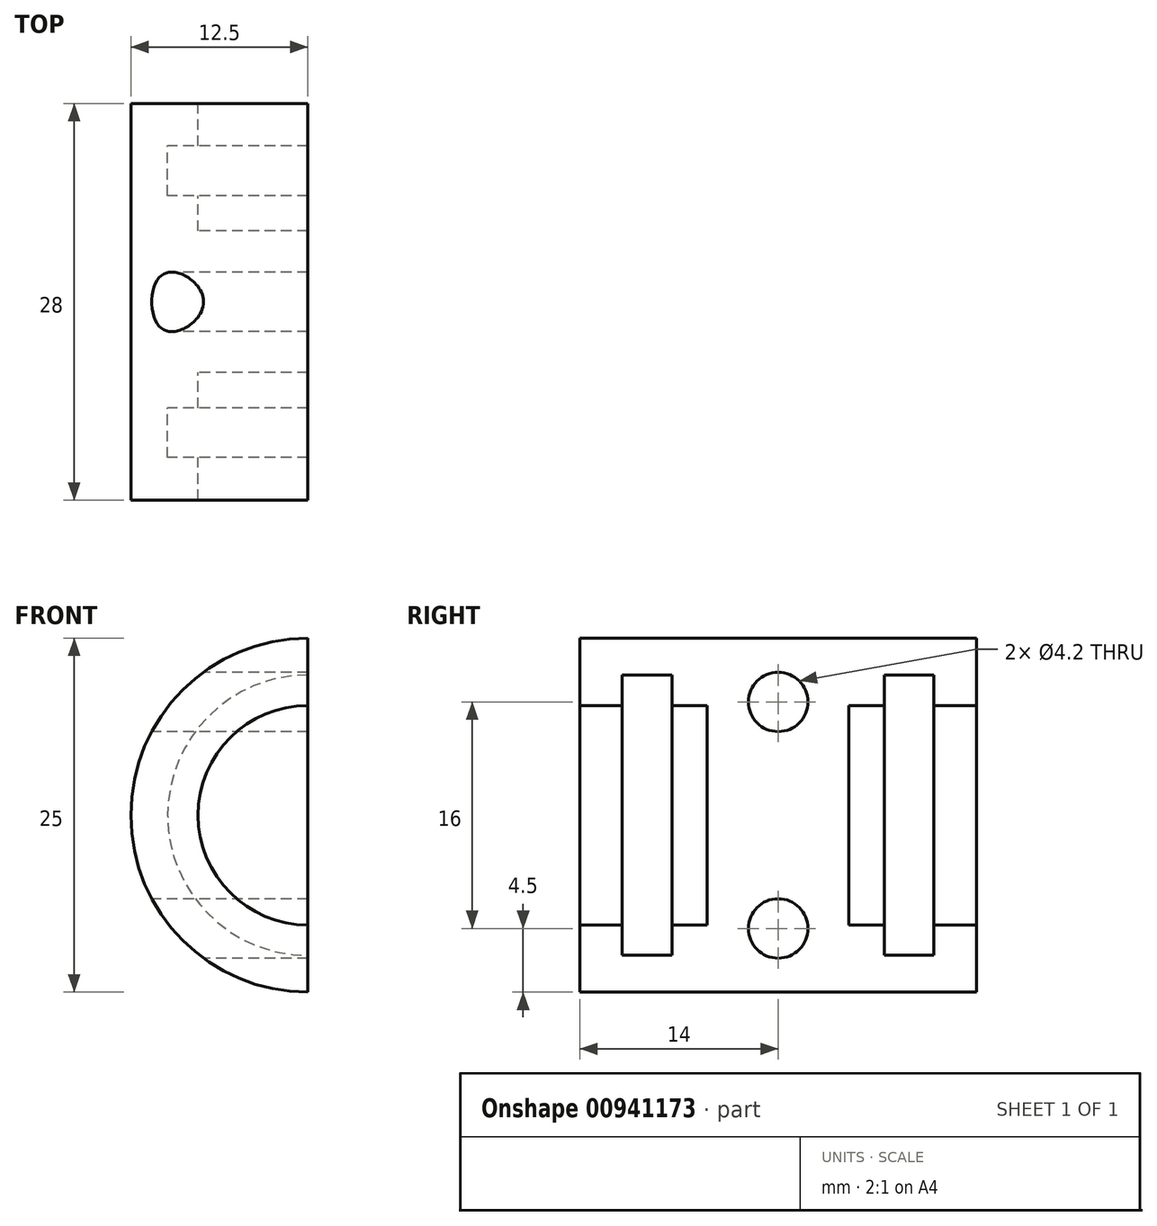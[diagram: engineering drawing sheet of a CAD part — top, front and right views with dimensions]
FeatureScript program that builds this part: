
annotation { "Feature Type Name" : "Feature", "Feature Type Description" : "" }
export const myFeature = defineFeature(function(context is Context, id is Id, definition is map)
    precondition{}
    {
        {
            var Q0;
            Q0=qCreatedBy(makeId("Front.planeOp"),FACE);
            var sketch = newSketch(context, id + "F0", { "sketchPlane" : qUnion([Q0])});
            skCircle(sketch, "E0", {"center": v(0, 0) * mm, "radius": 12.5 * mm});
            skCircle(sketch, "E1", {"center": v(0, 0) * mm, "radius": 7.75 * mm});
            skSolve(sketch);
        }
        {
            var Q0;
            Q0=makeQuery(id+"F0.imprint","IMPRINT",FACE,{"disambiguationData":[TD([[makeQuery(id+"F0.imprint","IMPRINT",EDGE,{"derivedFrom":sQuery(id+"F0.wireOp",EDGE,"E0")}),1.0]])]});
            extrude(context, id + "F1", {"entities" : qUnion([Q0]), "depth" : 28 * mm, "offsetDistance" : 25 * mm});
        }
        {
            var Q0;
            Q0=qCreatedBy(makeId("Right.planeOp"),FACE);
            var sketch = newSketch(context, id + "F2", { "sketchPlane" : qUnion([Q0])});
            skLineSegment(sketch, "E2.bottom", {"start": v(-21.5, 9.9) * mm, "end": v(-25, 9.9) * mm});
            skLineSegment(sketch, "E2.top", {"start": v(-21.5, -9.9) * mm, "end": v(-25, -9.9) * mm});
            skLineSegment(sketch, "E2.left", {"start": v(-21.5, 9.9) * mm, "end": v(-21.5, -9.9) * mm});
            skLineSegment(sketch, "E2.right", {"start": v(-25, 9.9) * mm, "end": v(-25, -9.9) * mm});
            skPoint(sketch, "E2.middle", {"position": v(-23.25, 0) * mm});
            skLineSegment(sketch, "E3.bottom", {"start": v(-3, 9.9) * mm, "end": v(-6.5, 9.9) * mm});
            skLineSegment(sketch, "E3.top", {"start": v(-3, -9.9) * mm, "end": v(-6.5, -9.9) * mm});
            skLineSegment(sketch, "E3.left", {"start": v(-3, 9.9) * mm, "end": v(-3, -9.9) * mm});
            skLineSegment(sketch, "E3.right", {"start": v(-6.5, 9.9) * mm, "end": v(-6.5, -9.9) * mm});
            skPoint(sketch, "E3.middle", {"position": v(-4.75, 0) * mm});
            skLineSegment(sketch, "E4", {"start": v(-23.25, 0) * mm, "end": v(21.1, 0) * mm});
            skLineSegment(sketch, "E5", {"start": v(21.1, 0) * mm, "end": v(-23.25, 0) * mm});
            skLineSegment(sketch, "E6", {"start": v(-34.97, 0) * mm, "end": v(-23.25, 0) * mm});
            skLineSegment(sketch, "E7", {"start": v(-32.13, 2.52) * mm, "end": v(11.78, 2.52) * mm});
            skSolve(sketch);
        }
        {
            var Q0;
            {var subQ0=sQuery(id+"F2.wireOp",EDGE,"E2.bottom");Q0=makeQuery(id+"F2.imprint","IMPRINT",FACE,{"disambiguationData":[TD([[makeQuery(id+"F2.imprint","IMPRINT",EDGE,{"derivedFrom":subQ0}),1.0]])]});}
            var Q1;
            {var subQ0=sQuery(id+"F2.wireOp",EDGE,"E3.bottom");Q1=makeQuery(id+"F2.imprint","IMPRINT",FACE,{"disambiguationData":[TD([[makeQuery(id+"F2.imprint","IMPRINT",EDGE,{"derivedFrom":subQ0}),1.0]])]});}
            var Q2;
            Q2=sQuery(id+"F2.wireOp",EDGE,"E6");
            revolve(context, id + "F3", {"operationType" : NewBodyOperationType.REMOVE, "surfaceOperationType" : NewSurfaceOperationType.NEW, "entities" : qUnion([Q0, Q1]), "axis" : qUnion([Q2]), "revolveType" : RevolveType.FULL, "oppositeDirection" : true});
        }
        {
            var Q0;
            Q0=makeQuery(id+"F1.opExtrude","CAP_FACE",FACE,{"disambiguationData":[OSD([sQuery(id+"F0.wireOp",EDGE,"E0"),sQuery(id+"F0.wireOp",EDGE,"E1")])],"isStart":false});
            var Q1;
            Q1=makeQuery(id+"F1.opExtrude","CAP_FACE",FACE,{"disambiguationData":[OSD([sQuery(id+"F0.wireOp",EDGE,"E0"),sQuery(id+"F0.wireOp",EDGE,"E1")])],"isStart":true});
            cPlane(context, id + "F4", {"entities" : qUnion([Q0, Q1]), "cplaneType" : CPlaneType.MID_PLANE, "offset" : 25 * mm, "width" : 150 * mm, "height" : 150 * mm});
        }
        {
            var Q0;
            Q0=qCreatedBy(id+"F4.planeOp",FACE);
            var sketch = newSketch(context, id + "F5", { "sketchPlane" : qUnion([Q0])});
            skCircle(sketch, "E8", {"center": v(0, 0) * mm, "radius": 8.5 * mm});
            skCircle(sketch, "E9", {"center": v(0, 0) * mm, "radius": 16.22 * mm});
            skSolve(sketch);
        }
        {
            var Q0;
            Q0=makeQuery(id+"F5.imprint","IMPRINT",FACE,{"disambiguationData":[TD([[makeQuery(id+"F5.imprint","IMPRINT",EDGE,{"derivedFrom":sQuery(id+"F5.wireOp",EDGE,"E8")}),1.0]])]});
            extrude(context, id + "F6", {"entities" : qUnion([Q0]), "operationType" : NewBodyOperationType.ADD, "endBound" : BoundingType.SYMMETRIC, "depth" : 10 * mm, "offsetDistance" : 25 * mm});
        }
        {
            var Q0;
            Q0=qCreatedBy(makeId("Right.planeOp"),FACE);
            var sketch = newSketch(context, id + "F7", { "sketchPlane" : qUnion([Q0])});
            skLineSegment(sketch, "E10", {"start": v(0, 0) * mm, "end": v(-28, 0) * mm});
            skLineSegment(sketch, "E11", {"start": v(-14, 0) * mm, "end": v(-14, 8) * mm});
            skLineSegment(sketch, "E12", {"start": v(-14, 8) * mm, "end": v(-14, 0) * mm});
            skLineSegment(sketch, "E13", {"start": v(-14, -8) * mm, "end": v(-14, 0) * mm});
            skCircle(sketch, "E14", {"center": v(-14, 8) * mm, "radius": 2.1 * mm});
            skCircle(sketch, "E15", {"center": v(-14, -8) * mm, "radius": 2.1 * mm});
            skSolve(sketch);
        }
        {
            var Q0;
            Q0 = qSketchRegion(id + "F7", true);
            extrude(context, id + "F8", {"entities" : qUnion([Q0]), "operationType" : NewBodyOperationType.REMOVE, "endBound" : BoundingType.SYMMETRIC, "depth" : 25 * mm, "offsetDistance" : 25 * mm});
        }
        {
            var Q0;
            Q0=makeQuery(id+"F1.opExtrude","CAP_FACE",FACE,{"disambiguationData":[OSD([sQuery(id+"F0.wireOp",EDGE,"E0"),sQuery(id+"F0.wireOp",EDGE,"E1")])],"isStart":false});
            var sketch = newSketch(context, id + "F9", { "sketchPlane" : qUnion([Q0])});
            skLineSegment(sketch, "E16", {"start": v(0, -2.16) * mm, "end": v(0, 25.02) * mm});
            skLineSegment(sketch, "E17", {"start": v(0, 25.02) * mm, "end": v(20.81, 25.02) * mm});
            skLineSegment(sketch, "E18", {"start": v(20.81, 25.02) * mm, "end": v(20.81, -22.7) * mm});
            skLineSegment(sketch, "E19", {"start": v(20.81, -22.7) * mm, "end": v(0, -22.7) * mm});
            skLineSegment(sketch, "E20", {"start": v(0, -22.7) * mm, "end": v(0, -2.16) * mm});
            skSolve(sketch);
        }
        {
            var Q0;
            {var subQ0=sQuery(id+"F9.wireOp",EDGE,"E16");var subQ1=makeQuery(id+"F1.opExtrude","CAP_EDGE",EDGE,{"disambiguationData":[OSD([sQuery(id+"F0.wireOp",EDGE,"E0")])],"isStart":false});var subQ2=makeQuery(id+"F9.imprint","INTERSECT",VERTEX,{"derivedFrom":[subQ1,subQ0]});Q0=makeQuery(id+"F9.imprint","IMPRINT",FACE,{"disambiguationData":[TD([[makeQuery(id+"F9.imprint","IMPRINT",EDGE,{"disambiguationData":[TD([[subQ2,1.0]])],"derivedFrom":subQ0}),-1.0]])]});}
            var Q1;
            {var subQ0=sQuery(id+"F9.wireOp",EDGE,"E20");var subQ1=sQuery(id+"F9.wireOp",EDGE,"E16");var subQ2=makeQuery(id+"F9.imprint","INTERSECT",VERTEX,{"derivedFrom":[subQ1,subQ0]});Q1=makeQuery(id+"F9.imprint","IMPRINT",FACE,{"disambiguationData":[TD([[makeQuery(id+"F9.imprint","IMPRINT",EDGE,{"disambiguationData":[TD([[subQ2,-1.0]])],"derivedFrom":subQ1}),-1.0]])]});}
            extrude(context, id + "F10", {"entities" : qUnion([Q0, Q1]), "operationType" : NewBodyOperationType.REMOVE, "oppositeDirection" : true, "depth" : 30 * mm, "offsetDistance" : 25 * mm});
        }
    });
